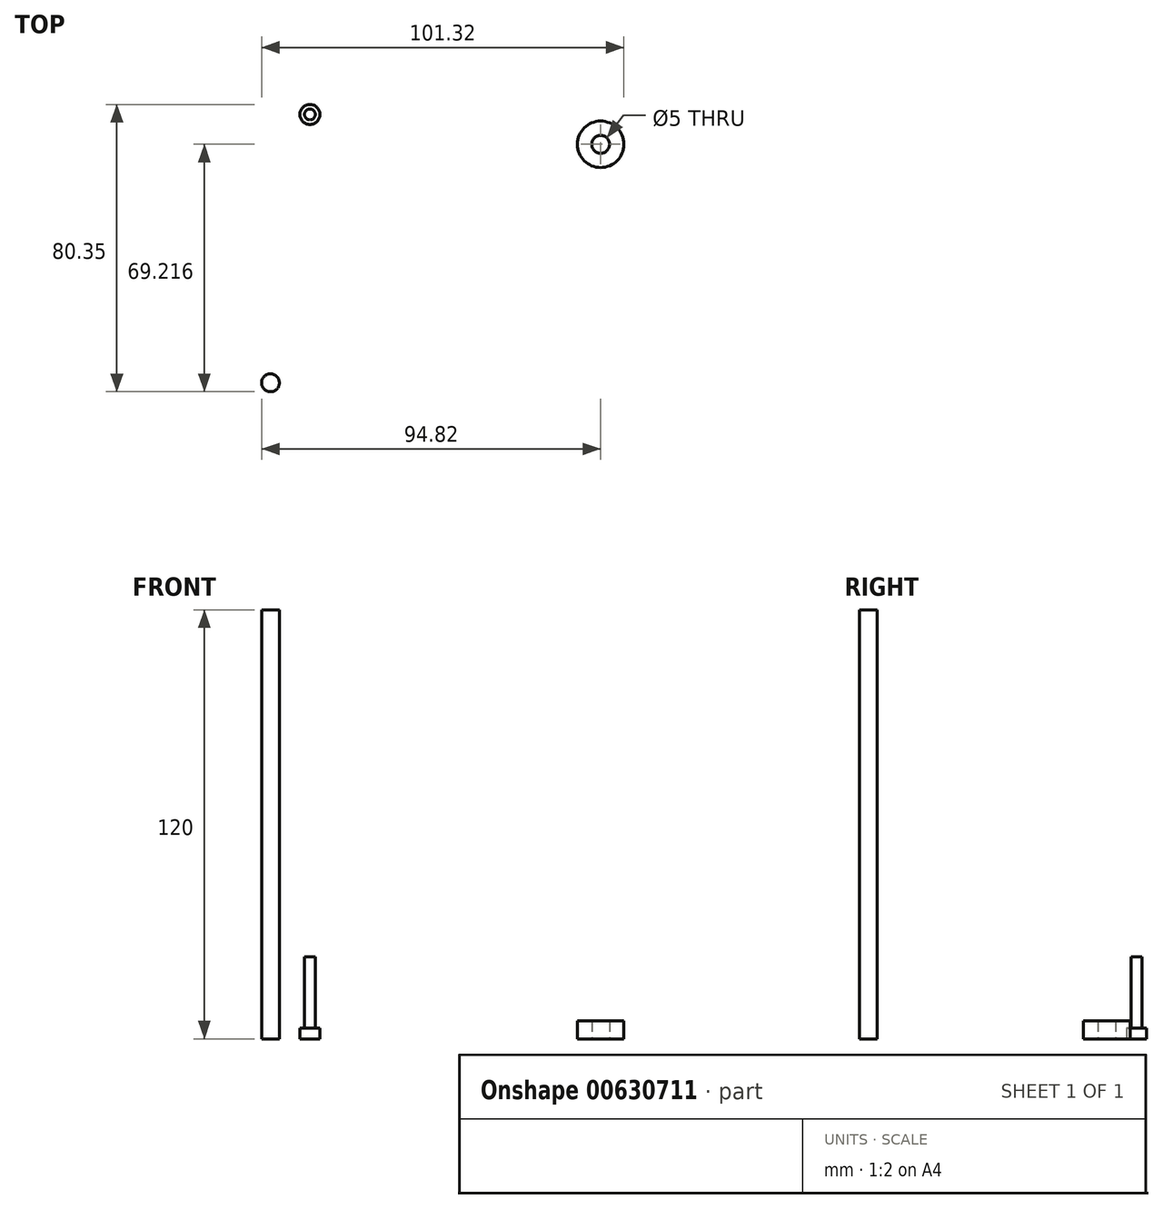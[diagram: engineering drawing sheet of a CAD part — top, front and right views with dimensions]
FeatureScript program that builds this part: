
annotation { "Feature Type Name" : "Feature", "Feature Type Description" : "" }
export const myFeature = defineFeature(function(context is Context, id is Id, definition is map)
    precondition{}
    {
        {
            var Q0;
            Q0=qCreatedBy(makeId("Top.planeOp"),FACE);
            var sketch = newSketch(context, id + "F0", { "sketchPlane" : qUnion([Q0])});
            skCircle(sketch, "E0", {"center": v(-48.84, 40.4) * mm, "radius": 2.8 * mm});
            skSolve(sketch);
        }
        {
            var Q0;
            Q0=makeQuery(id+"F0.imprint","IMPRINT",FACE,{"disambiguationData":[TD([[makeQuery(id+"F0.imprint","IMPRINT",EDGE,{"derivedFrom":sQuery(id+"F0.wireOp",EDGE,"E0")}),1.0]])]});
            extrude(context, id + "F1", {"entities" : qUnion([Q0]), "depth" : 3 * mm, "offsetDistance" : 25 * mm});
        }
        {
            var Q0;
            Q0=makeQuery(id+"F1.opExtrude","CAP_FACE",FACE,{"disambiguationData":[OSD([sQuery(id+"F0.wireOp",EDGE,"E0")])],"isStart":false});
            var sketch = newSketch(context, id + "F2", { "sketchPlane" : qUnion([Q0])});
            skCircle(sketch, "E1", {"center": v(-48.84, 40.4) * mm, "radius": 1.5 * mm});
            skSolve(sketch);
        }
        {
            var Q0;
            Q0 = qSketchRegion(id + "F2", true);
            extrude(context, id + "F3", {"entities" : qUnion([Q0]), "operationType" : NewBodyOperationType.ADD, "depth" : 20 * mm, "offsetDistance" : 25 * mm});
        }
        {
            var Q0;
            Q0=qCreatedBy(makeId("Top.planeOp"),FACE);
            var sketch = newSketch(context, id + "F4", { "sketchPlane" : qUnion([Q0])});
            skCircle(sketch, "E2", {"center": v(32.46, 32.08) * mm, "radius": 6.5 * mm});
            skCircle(sketch, "E3", {"center": v(32.46, 32.08) * mm, "radius": 2.5 * mm});
            skSolve(sketch);
        }
        {
            var Q0;
            Q0 = qSketchRegion(id + "F4", true);
            extrude(context, id + "F5", {"entities" : qUnion([Q0]), "depth" : 5 * mm, "offsetDistance" : 25 * mm});
        }
        {
            var Q0;
            Q0=qCreatedBy(makeId("Top.planeOp"),FACE);
            var sketch = newSketch(context, id + "F6", { "sketchPlane" : qUnion([Q0])});
            skCircle(sketch, "E4", {"center": v(-59.86, -34.64) * mm, "radius": 2.5 * mm});
            skSolve(sketch);
        }
        {
            var Q0;
            Q0=makeQuery(id+"F6.imprint","IMPRINT",FACE,{"disambiguationData":[TD([[makeQuery(id+"F6.imprint","IMPRINT",EDGE,{"derivedFrom":sQuery(id+"F6.wireOp",EDGE,"E4")}),1.0]])]});
            extrude(context, id + "F7", {"entities" : qUnion([Q0]), "depth" : 120 * mm, "offsetDistance" : 25 * mm});
        }
    });
